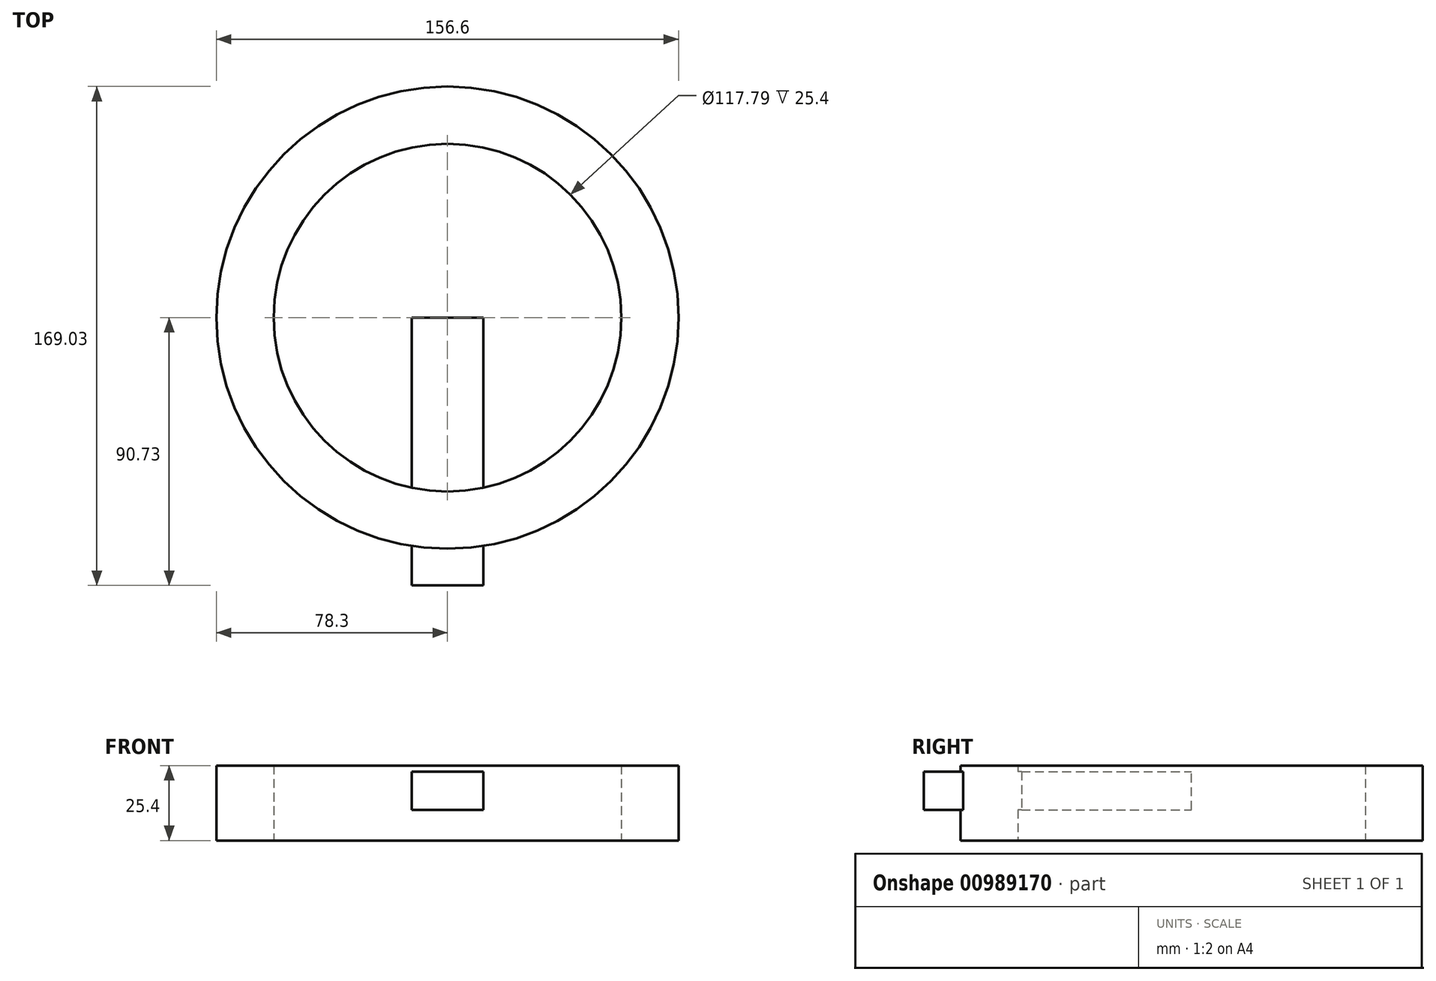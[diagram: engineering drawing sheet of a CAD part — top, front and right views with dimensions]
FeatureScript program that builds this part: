
annotation { "Feature Type Name" : "Feature", "Feature Type Description" : "" }
export const myFeature = defineFeature(function(context is Context, id is Id, definition is map)
    precondition{}
    {
        {
            var Q0;
            Q0=qCreatedBy(makeId("Top.planeOp"),FACE);
            var sketch = newSketch(context, id + "F0", { "sketchPlane" : qUnion([Q0])});
            skCircle(sketch, "E0", {"center": v(0, 0) * mm, "radius": 78.3 * mm});
            skCircle(sketch, "E1", {"center": v(0, 0) * mm, "radius": 58.9 * mm});
            skSolve(sketch);
        }
        {
            var Q0;
            Q0 = qSketchRegion(id + "F0", true);
            extrude(context, id + "F1", {"entities" : qUnion([Q0]), "depth" : 25.4 * mm, "offsetDistance" : 25.4 * mm});
        }
        {
            var Q0;
            Q0=qCreatedBy(makeId("Front.planeOp"),FACE);
            var sketch = newSketch(context, id + "F2", { "sketchPlane" : qUnion([Q0])});
            skLineSegment(sketch, "E2.bottom", {"start": v(12.16, 10.42) * mm, "end": v(-12.16, 10.42) * mm});
            skLineSegment(sketch, "E2.top", {"start": v(12.16, 23.35) * mm, "end": v(-12.16, 23.35) * mm});
            skLineSegment(sketch, "E2.left", {"start": v(12.16, 10.42) * mm, "end": v(12.16, 23.35) * mm});
            skLineSegment(sketch, "E2.right", {"start": v(-12.16, 10.42) * mm, "end": v(-12.16, 23.35) * mm});
            skPoint(sketch, "E2.middle", {"position": v(0, 16.89) * mm});
            skSolve(sketch);
        }
        {
            var Q0;
            Q0 = qSketchRegion(id + "F2", true);
            extrude(context, id + "F3", {"entities" : qUnion([Q0]), "operationType" : NewBodyOperationType.ADD, "depth" : 90.73 * mm, "offsetDistance" : 25.4 * mm});
        }
    });
